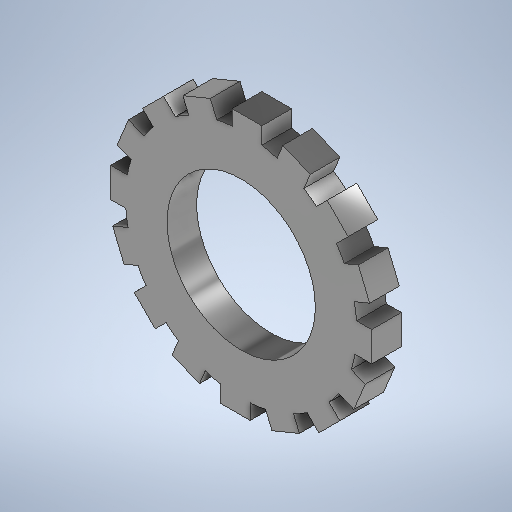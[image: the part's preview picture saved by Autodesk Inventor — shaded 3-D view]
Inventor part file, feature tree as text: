
AUTODESK INVENTOR PART (.ipt)
format: ipt  version: 2025.2 (Build 292293000, 293)  size: 368,640 bytes
history: native  units: in
note: dims shown in document units (in); Inventor stores cm internally (conversion verified against a paired STEP export)
features: extrude x2, sketch x2, plane x1, pattern_circular x1, other x1
ambient origin geometry x8: Origin, YZ Plane, XZ Plane, XY Plane, X Axis, Y Axis, Z Axis, Center Point
bodies: Solid1 (feature_tree)
feature tree (7):
  extrude  "Extrusion1"  Depth=3.0709in
  plane  "Work Plane1"
  extrude  "Extrusion2"  Depth=1.5354in
  pattern_circular  "Circular Pattern1"  [2 undecoded]
  sketch  "Sketch1"  dims[d7=1.9685in d8=3.0709in]
  other  "Image1"
  sketch  "Sketch2"  dims[d9=0.3937in d10=0.0in d12=1.5354in d13=0.3937in d14=0.3937in d15=0.1969in d16=0.1969in d17=0.0in d18=0.0in d19=6.2992in d20=360.0deg]
note: 2 required parameter values undecoded (feature->parameter linkage not recoverable at this tier; creation-order binding heuristic only, values carry confidence <= 0.55)
